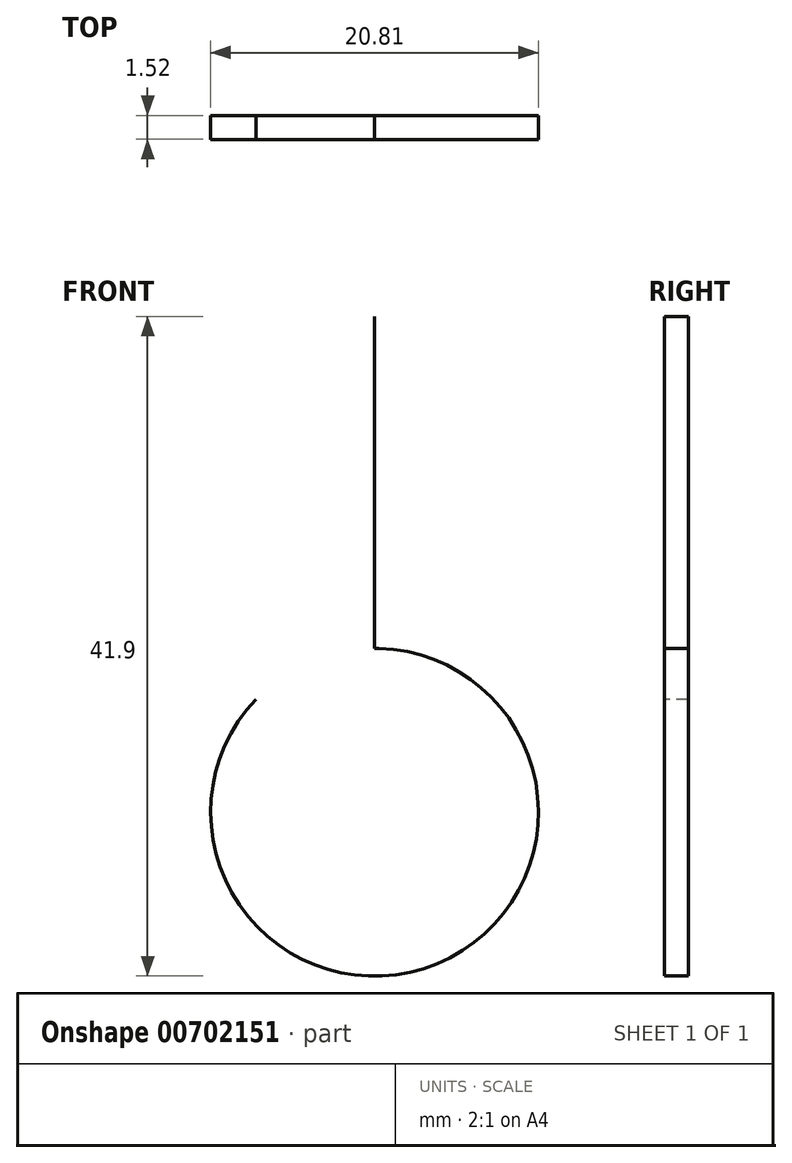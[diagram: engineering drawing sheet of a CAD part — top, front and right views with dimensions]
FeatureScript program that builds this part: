
annotation { "Feature Type Name" : "Feature", "Feature Type Description" : "" }
export const myFeature = defineFeature(function(context is Context, id is Id, definition is map)
    precondition{}
    {
        {
            var Q0;
            Q0=qCreatedBy(makeId("Front.planeOp"),FACE);
            var sketch = newSketch(context, id + "F0", { "sketchPlane" : qUnion([Q0])});
            skLineSegment(sketch, "E0", {"start": v(-39.24, 49.4) * mm, "end": v(-39.24, 28.32) * mm});
            skLineSegment(sketch, "E1", {"start": v(-39.24, 28.32) * mm, "end": v(-38.96, 28.31) * mm});
            skArc(sketch, "E2", {"start": v(-46.78, 25.09) * mm, "mid": v(-35.27, 8.29) * mm, "end": v(-38.96, 28.31) * mm});
            skSolve(sketch);
        }
        {
            var Q0;
            Q0=sQuery(id+"F0.wireOp",EDGE,"E2");
            var Q1;
            Q1=sQuery(id+"F0.wireOp",EDGE,"E1");
            var Q2;
            Q2=sQuery(id+"F0.wireOp",EDGE,"E0");
            extrude(context, id + "F1", {"bodyType" : ToolBodyType.SURFACE, "surfaceEntities" : qUnion([Q0, Q1, Q2]), "depth" : 1.52 * mm, "offsetDistance" : 25.4 * mm});
        }
    });
